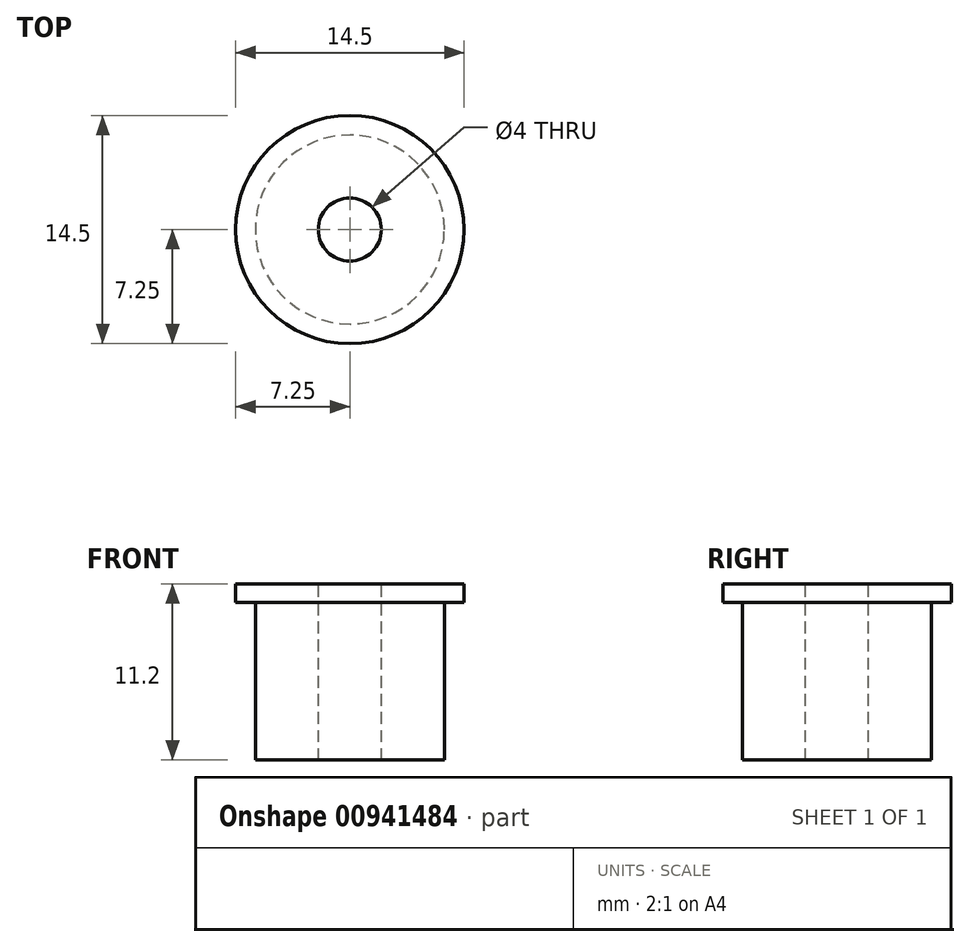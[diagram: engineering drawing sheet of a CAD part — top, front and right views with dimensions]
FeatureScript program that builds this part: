
annotation { "Feature Type Name" : "Feature", "Feature Type Description" : "" }
export const myFeature = defineFeature(function(context is Context, id is Id, definition is map)
    precondition{}
    {
        {
            var Q0;
            Q0=qCreatedBy(makeId("Top.planeOp"),FACE);
            var sketch = newSketch(context, id + "F0", { "sketchPlane" : qUnion([Q0])});
            skCircle(sketch, "E0", {"center": v(0, 0) * mm, "radius": 6 * mm});
            skSolve(sketch);
        }
        {
            var Q0;
            Q0=makeQuery(id+"F0.imprint","IMPRINT",FACE,{"disambiguationData":[TD([[makeQuery(id+"F0.imprint","IMPRINT",EDGE,{"derivedFrom":sQuery(id+"F0.wireOp",EDGE,"E0")}),1.0]])]});
            extrude(context, id + "F1", {"entities" : qUnion([Q0]), "flatOperationType" : FlatOperationType.REMOVE, "depth" : 10 * mm, "offsetDistance" : 25 * mm, "domain" : OperationDomain.MODEL});
        }
        {
            var Q0;
            Q0=makeQuery(id+"F1.opExtrude","CAP_FACE",FACE,{"disambiguationData":[OSD([sQuery(id+"F0.wireOp",EDGE,"E0")])],"isStart":false});
            var sketch = newSketch(context, id + "F2", { "sketchPlane" : qUnion([Q0])});
            skCircle(sketch, "E1", {"center": v(0, 0) * mm, "radius": 7.25 * mm});
            skSolve(sketch);
        }
        {
            var Q0;
            Q0=makeQuery(id+"F2.imprint","IMPRINT",FACE,{"disambiguationData":[TD([[makeQuery(id+"F2.imprint","IMPRINT",EDGE,{"derivedFrom":sQuery(id+"F2.wireOp",EDGE,"E1")}),1.0]])]});
            var Q1;
            Q1=makeQuery(id+"F2.imprint","IMPRINT",FACE,{"disambiguationData":[TD([[makeQuery(id+"F2.imprint","IMPRINT",EDGE,{"derivedFrom":makeQuery(id+"F1.opExtrude","CAP_EDGE",EDGE,{"disambiguationData":[OSD([sQuery(id+"F0.wireOp",EDGE,"E0")])],"isStart":false})}),1.0]])]});
            extrude(context, id + "F3", {"entities" : qUnion([Q0, Q1]), "operationType" : NewBodyOperationType.ADD, "flatOperationType" : FlatOperationType.REMOVE, "depth" : 1.2 * mm, "offsetDistance" : 25 * mm, "domain" : OperationDomain.MODEL});
        }
        {
            var Q0;
            Q0=makeQuery(id+"F3.opExtrude","CAP_FACE",FACE,{"disambiguationData":[OSD([sQuery(id+"F2.wireOp",EDGE,"E1")])],"isStart":false});
            var sketch = newSketch(context, id + "F4", { "sketchPlane" : qUnion([Q0])});
            skCircle(sketch, "E2", {"center": v(0, 0) * mm, "radius": 2 * mm});
            skSolve(sketch);
        }
        {
            var Q0;
            Q0=makeQuery(id+"F4.imprint","IMPRINT",FACE,{"disambiguationData":[TD([[makeQuery(id+"F4.imprint","IMPRINT",EDGE,{"derivedFrom":sQuery(id+"F4.wireOp",EDGE,"E2")}),1.0]])]});
            extrude(context, id + "F5", {"entities" : qUnion([Q0]), "operationType" : NewBodyOperationType.REMOVE, "oppositeDirection" : true, "depth" : 25 * mm, "offsetDistance" : 25 * mm});
        }
    });
